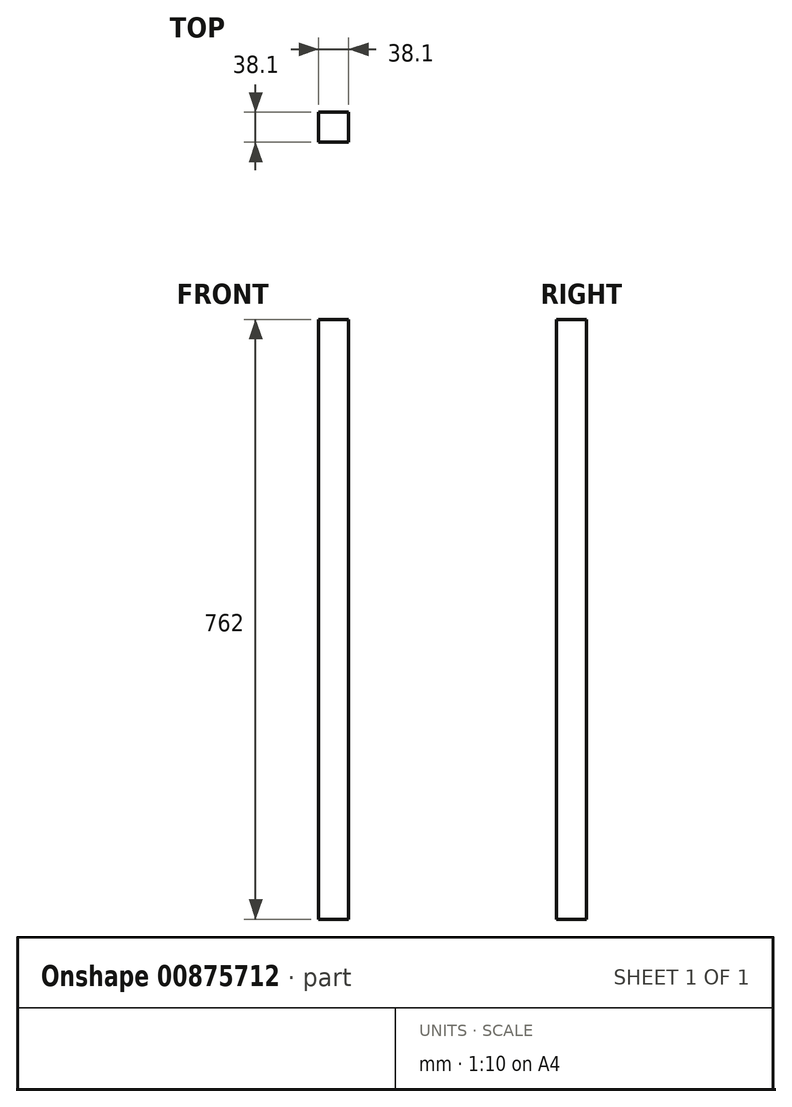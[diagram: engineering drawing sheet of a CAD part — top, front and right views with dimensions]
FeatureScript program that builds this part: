
annotation { "Feature Type Name" : "Feature", "Feature Type Description" : "" }
export const myFeature = defineFeature(function(context is Context, id is Id, definition is map)
    precondition{}
    {
        {
            var Q0;
            Q0=qCreatedBy(makeId("Top.planeOp"),FACE);
            var sketch = newSketch(context, id + "F0", { "sketchPlane" : qUnion([Q0])});
            skLineSegment(sketch, "E0.bottom", {"start": v(19.05, -19.05) * mm, "end": v(-19.05, -19.05) * mm});
            skLineSegment(sketch, "E0.top", {"start": v(19.05, 19.05) * mm, "end": v(-19.05, 19.05) * mm});
            skLineSegment(sketch, "E0.left", {"start": v(19.05, -19.05) * mm, "end": v(19.05, 19.05) * mm});
            skLineSegment(sketch, "E0.right", {"start": v(-19.05, -19.05) * mm, "end": v(-19.05, 19.05) * mm});
            skPoint(sketch, "E0.middle", {"position": v(0, 0) * mm});
            skSolve(sketch);
        }
        {
            var Q0;
            Q0 = qSketchRegion(id + "F0", true);
            extrude(context, id + "F1", {"entities" : qUnion([Q0]), "endBound" : BoundingType.SYMMETRIC, "depth" : 762 * mm, "offsetDistance" : 25.4 * mm});
        }
    });
